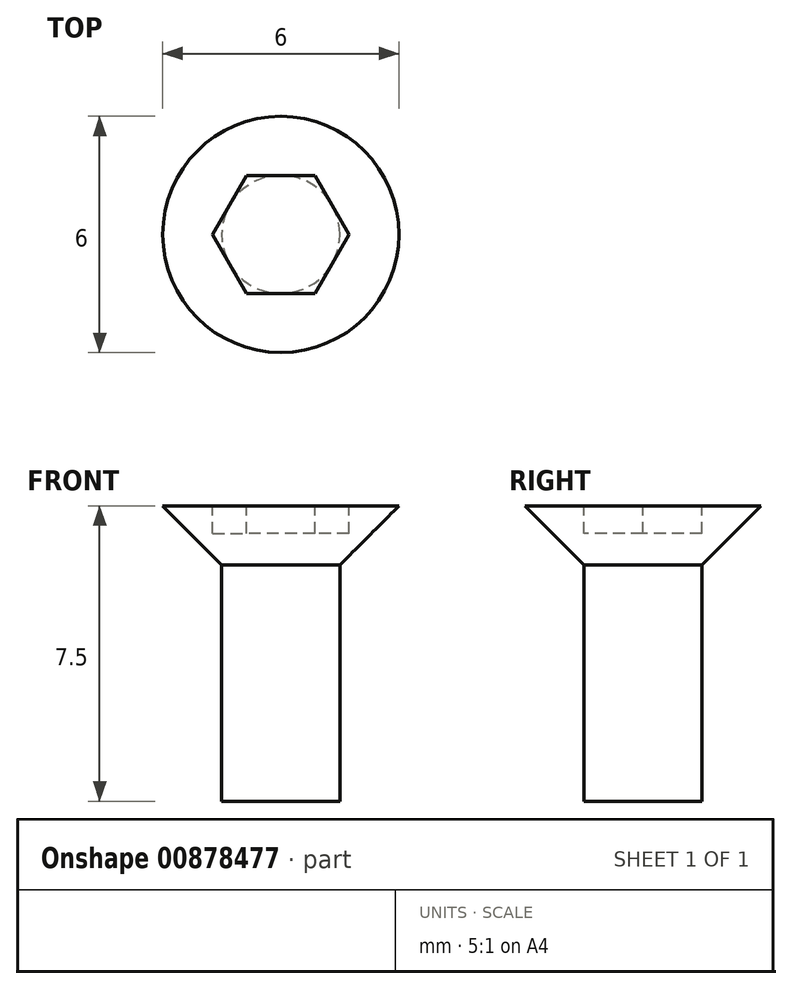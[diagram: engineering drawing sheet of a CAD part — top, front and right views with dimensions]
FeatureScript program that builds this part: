
annotation { "Feature Type Name" : "Feature", "Feature Type Description" : "" }
export const myFeature = defineFeature(function(context is Context, id is Id, definition is map)
    precondition{}
    {
        {
            var Q0;
            Q0=qCreatedBy(makeId("Front.planeOp"),FACE);
            var sketch = newSketch(context, id + "F0", { "sketchPlane" : qUnion([Q0])});
            skLineSegment(sketch, "E0.top", {"start": v(-1.5, -6) * mm, "end": v(1.5, -6) * mm});
            skLineSegment(sketch, "E0.left", {"start": v(-1.5, 0) * mm, "end": v(-1.5, -6) * mm});
            skLineSegment(sketch, "E0.right", {"start": v(1.5, 0) * mm, "end": v(1.5, -6) * mm});
            skLineSegment(sketch, "E1", {"start": v(-1.5, 0) * mm, "end": v(-3, 1.5) * mm});
            skLineSegment(sketch, "E2", {"start": v(-3, 1.5) * mm, "end": v(3, 1.5) * mm});
            skLineSegment(sketch, "E3", {"start": v(3, 1.5) * mm, "end": v(1.5, 0) * mm});
            skLineSegment(sketch, "E4", {"start": v(0, 4.22) * mm, "end": v(0, -12.62) * mm});
            skSolve(sketch);
        }
        {
            var Q0;
            {var subQ1=sQuery(id+"F0.wireOp",EDGE,"E0.left");Q0=makeQuery(id+"F0.imprint","IMPRINT",FACE,{"disambiguationData":[TD([[makeQuery(id+"F0.imprint","IMPRINT",EDGE,{"derivedFrom":subQ1}),1.0]])]});}
            var Q1;
            Q1=sQuery(id+"F0.wireOp",EDGE,"E4");
            revolve(context, id + "F1", {"surfaceOperationType" : NewSurfaceOperationType.NEW, "entities" : qUnion([Q0]), "axis" : qUnion([Q1]), "revolveType" : RevolveType.FULL});
        }
        {
            var Q0;
            Q0=makeQuery(id+"F1.opRevolve","SWEPT_FACE",FACE,{"disambiguationData":[OSD([sQuery(id+"F0.wireOp",EDGE,"E2")])]});
            var sketch = newSketch(context, id + "F2", { "sketchPlane" : qUnion([Q0])});
            skCircle(sketch, "E5.cCircle", {"center": v(0, 0) * mm, "radius": 1.5 * mm, "construction": true});
            skLineSegment(sketch, "E5.0", {"start": v(0.87, -1.5) * mm, "end": v(-0.87, -1.5) * mm});
            skLineSegment(sketch, "E5.1", {"start": v(-0.87, -1.5) * mm, "end": v(-1.73, 0) * mm});
            skLineSegment(sketch, "E5.2", {"start": v(-1.73, 0) * mm, "end": v(-0.87, 1.5) * mm});
            skLineSegment(sketch, "E5.3", {"start": v(-0.87, 1.5) * mm, "end": v(0.87, 1.5) * mm});
            skLineSegment(sketch, "E5.4", {"start": v(0.87, 1.5) * mm, "end": v(1.73, 0) * mm});
            skLineSegment(sketch, "E5.5", {"start": v(1.73, 0) * mm, "end": v(0.87, -1.5) * mm});
            skPoint(sketch, "E5.0.midPoint", {"position": v(0, -1.5) * mm});
            skSolve(sketch);
        }
        {
            var Q0;
            Q0 = qSketchRegion(id + "F2", true);
            extrude(context, id + "F3", {"entities" : qUnion([Q0]), "operationType" : NewBodyOperationType.REMOVE, "oppositeDirection" : true, "depth" : 0.7 * mm, "offsetDistance" : 25 * mm});
        }
    });
